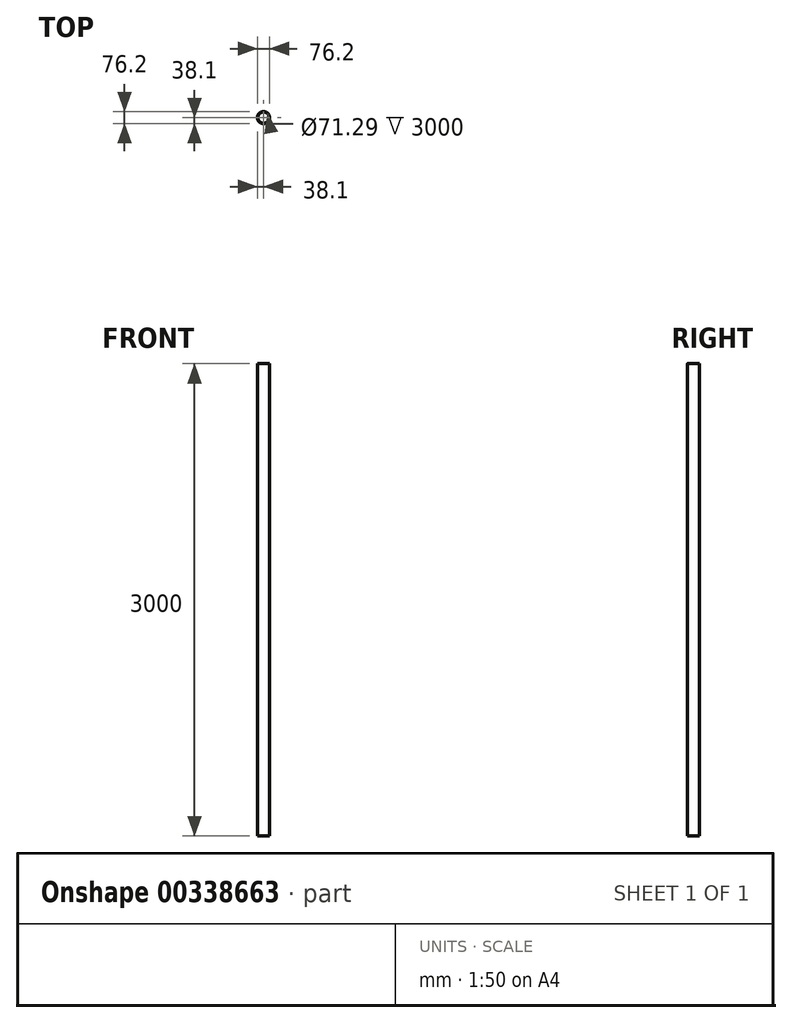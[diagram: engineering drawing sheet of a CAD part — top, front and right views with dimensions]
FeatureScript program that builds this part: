
annotation { "Feature Type Name" : "Feature", "Feature Type Description" : "" }
export const myFeature = defineFeature(function(context is Context, id is Id, definition is map)
    precondition{}
    {
        {
            var Q0;
            Q0=qCreatedBy(makeId("Top.planeOp"),FACE);
            var sketch = newSketch(context, id + "F0", { "sketchPlane" : qUnion([Q0])});
            skCircle(sketch, "E0", {"center": v(0, 0) * mm, "radius": 38.1 * mm});
            skCircle(sketch, "E1", {"center": v(0, 0) * mm, "radius": 35.64 * mm});
            skSolve(sketch);
        }
        {
            var Q0;
            Q0 = qSketchRegion(id + "F0", true);
            extrude(context, id + "F1", {"entities" : qUnion([Q0]), "depth" : 3000 * mm});
        }
    });
